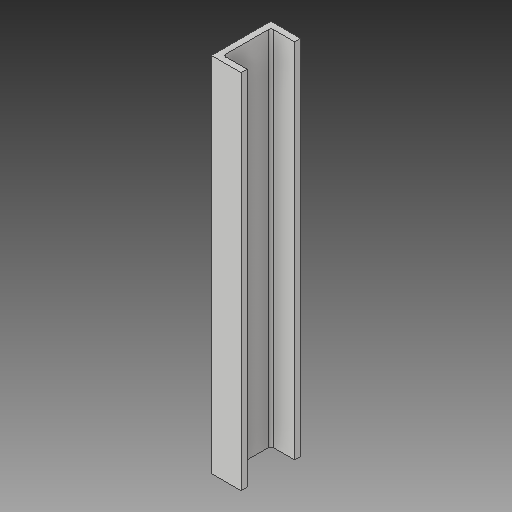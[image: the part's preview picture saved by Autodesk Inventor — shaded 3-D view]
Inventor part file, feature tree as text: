
AUTODESK INVENTOR PART (.ipt)
format: ipt  version: 2019 (Build 230136000, 136)  size: 99,328 bytes
history: native  units: in
note: dims shown in document units (in); Inventor stores cm internally (conversion verified against a paired STEP export)
features: other x3, sketch x2
ambient origin geometry x8: Origin, YZ Plane, XZ Plane, XY Plane, X Axis, Y Axis, Z Axis, Center Point
bodies: Solid1 (feature_tree)
feature tree (5):
  other  "Base3.ipt"
  other  "Solid1::Base3.ipt"
  other  "TaggingFeature1"
  sketch  "Sketch1"  dims[d0=0.3937in]
  sketch  "Sketch2"
